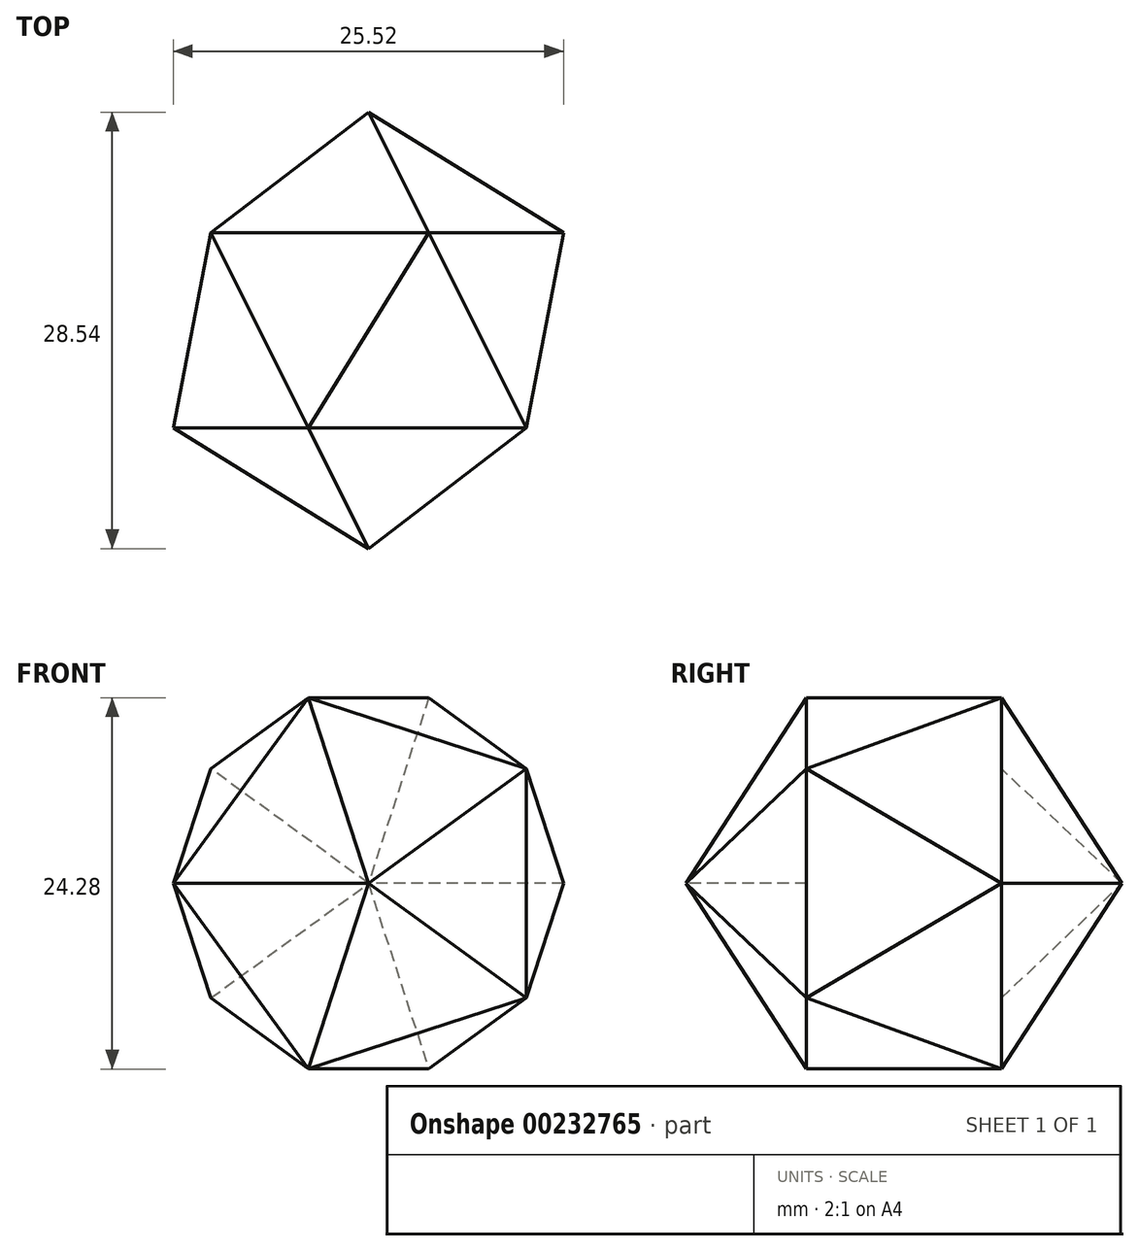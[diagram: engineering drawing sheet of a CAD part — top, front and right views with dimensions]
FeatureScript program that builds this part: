
annotation { "Feature Type Name" : "Feature", "Feature Type Description" : "" }
export const myFeature = defineFeature(function(context is Context, id is Id, definition is map)
    precondition{}
    {
        {
            var Q0;
            Q0=qCreatedBy(makeId("Front.planeOp"),FACE);
            var sketch = newSketch(context, id + "F0", { "sketchPlane" : qUnion([Q0])});
            skCircle(sketch, "E0.cCircle", {"center": v(0, 0) * mm, "radius": 10.32 * mm, "construction": true});
            skLineSegment(sketch, "E0.0", {"start": v(10.32, 7.5) * mm, "end": v(10.32, -7.5) * mm});
            skLineSegment(sketch, "E0.1", {"start": v(10.32, -7.5) * mm, "end": v(-3.94, -12.14) * mm});
            skLineSegment(sketch, "E0.2", {"start": v(-3.94, -12.14) * mm, "end": v(-12.76, 0) * mm});
            skLineSegment(sketch, "E0.3", {"start": v(-12.76, 0) * mm, "end": v(-3.94, 12.14) * mm});
            skLineSegment(sketch, "E0.4", {"start": v(-3.94, 12.14) * mm, "end": v(10.32, 7.5) * mm});
            skPoint(sketch, "E0.0.midPoint", {"position": v(10.32, 0) * mm});
            skSolve(sketch);
        }
        {
            var Q0;
            Q0=qCreatedBy(makeId("Top.planeOp"),FACE);
            var sketch = newSketch(context, id + "F1", { "sketchPlane" : qUnion([Q0])});
            skLineSegment(sketch, "E1", {"start": v(0, -12.43) * mm, "end": v(0, 41.06) * mm, "construction": true});
            skSolve(sketch);
        }
        {
            var Q0;
            Q0=sQuery(id+"F0.wireOp",VERTEX,"E0.1.start");
            var Q1;
            Q1=sQuery(id+"F0.wireOp",VERTEX,"E0.cCircle.center");
            var Q2;
            Q2=sQuery(id+"F1.wireOp",VERTEX,"E1.start");
            cPlane(context, id + "F2", {"entities" : qUnion([Q0, Q1, Q2]), "cplaneType" : CPlaneType.THREE_POINT, "offset" : 25 * mm, "width" : 150 * mm, "height" : 150 * mm});
        }
        {
            var Q0;
            Q0=qCreatedBy(id+"F2.planeOp",FACE);
            var sketch = newSketch(context, id + "F3", { "sketchPlane" : qUnion([Q0])});
            skPoint(sketch, "E2.0", {"position": v(12.76, 0) * mm});
            skLineSegment(sketch, "E3", {"start": v(12.76, 0) * mm, "end": v(0, 7.89) * mm});
            skLineSegment(sketch, "E4.0", {"start": v(0, 12.43) * mm, "end": v(0, -41.06) * mm, "construction": true});
            skSolve(sketch);
        }
        {
            var Q0;
            Q0=qCreatedBy(id+"F2.planeOp",FACE);
            var sketch = newSketch(context, id + "F4", { "sketchPlane" : qUnion([Q0])});
            skPoint(sketch, "E5.1", {"position": v(0, 7.89) * mm});
            skLineSegment(sketch, "E6.0", {"start": v(0, 12.43) * mm, "end": v(0, -41.06) * mm, "construction": true});
            skArc(sketch, "E7", {"start": v(0, -20.65) * mm, "mid": v(14.27, -6.38) * mm, "end": v(0, 7.89) * mm});
            skLineSegment(sketch, "E8", {"start": v(0, 7.89) * mm, "end": v(0, -20.65) * mm});
            skLineSegment(sketch, "E9", {"start": v(23.46, 5.35) * mm, "end": v(-22.52, -17.64) * mm, "construction": true});
            skSolve(sketch);
        }
        {
            var Q0;
            Q0 = qSketchRegion(id + "F4", true);
            var Q1;
            Q1=sQuery(id+"F4.wireOp",EDGE,"E6.0");
            revolve(context, id + "F5", {"entities" : qUnion([Q0]), "axis" : qUnion([Q1]), "revolveType" : RevolveType.FULL});
        }
        {
            var Q0;
            Q0=sQuery(id+"F3.wireOp",VERTEX,"E2.0");
            var Q1;
            Q1=sQuery(id+"F3.wireOp",VERTEX,"E3.end");
            var Q2;
            Q2=sQuery(id+"F0.wireOp",VERTEX,"E0.4.start");
            cPlane(context, id + "F6", {"entities" : qUnion([Q0, Q1, Q2]), "cplaneType" : CPlaneType.THREE_POINT, "offset" : 25 * mm, "width" : 150 * mm, "height" : 150 * mm});
        }
        {
            var Q0;
            Q0=qCreatedBy(id+"F6.planeOp",FACE);
            var sketch = newSketch(context, id + "F7", { "sketchPlane" : qUnion([Q0])});
            skPoint(sketch, "E10.0", {"position": v(5.7, 0) * mm});
            skPoint(sketch, "E11.0", {"position": v(-2.65, -6.07) * mm});
            skCircle(sketch, "E12.cCircle", {"center": v(5.7, 0) * mm, "radius": 10.32 * mm, "construction": true});
            skLineSegment(sketch, "E12.0", {"start": v(1.76, -12.14) * mm, "end": v(-7.05, 0) * mm});
            skLineSegment(sketch, "E12.1", {"start": v(-7.05, 0) * mm, "end": v(1.76, 12.14) * mm});
            skLineSegment(sketch, "E12.2", {"start": v(1.76, 12.14) * mm, "end": v(16.03, 7.5) * mm});
            skLineSegment(sketch, "E12.3", {"start": v(16.03, 7.5) * mm, "end": v(16.03, -7.5) * mm});
            skLineSegment(sketch, "E12.4", {"start": v(16.03, -7.5) * mm, "end": v(1.76, -12.14) * mm});
            skSolve(sketch);
        }
        {
            var Q0;
            Q0=sQuery(id+"F3.wireOp",VERTEX,"E2.0");
            var Q1;
            Q1=sQuery(id+"F7.wireOp",VERTEX,"E12.0.end");
            var Q2;
            Q2=sQuery(id+"F0.wireOp",VERTEX,"E0.3.start");
            cPlane(context, id + "F8", {"entities" : qUnion([Q0, Q1, Q2]), "cplaneType" : CPlaneType.THREE_POINT, "offset" : 25 * mm, "width" : 150 * mm, "height" : 150 * mm});
        }
        {
            var Q0;
            Q0=qCreatedBy(id+"F8.planeOp",FACE);
            var sketch = newSketch(context, id + "F9", { "sketchPlane" : qUnion([Q0])});
            skPoint(sketch, "E13.0", {"position": v(6.38, -1.75) * mm});
            skPoint(sketch, "E13.1", {"position": v(1.01, -6.98) * mm});
            skPoint(sketch, "E14.0", {"position": v(-0.82, 5.65) * mm});
            skCircle(sketch, "E15.cCircle", {"center": v(-0.82, 5.65) * mm, "radius": 10.32 * mm, "construction": true});
            skLineSegment(sketch, "E15.0", {"start": v(11.76, 3.5) * mm, "end": v(1.01, -6.98) * mm});
            skLineSegment(sketch, "E15.1", {"start": v(1.01, -6.98) * mm, "end": v(-12.26, 0) * mm});
            skLineSegment(sketch, "E15.2", {"start": v(-12.26, 0) * mm, "end": v(-9.73, 14.78) * mm});
            skLineSegment(sketch, "E15.3", {"start": v(-9.73, 14.78) * mm, "end": v(5.12, 16.94) * mm});
            skLineSegment(sketch, "E15.4", {"start": v(5.12, 16.94) * mm, "end": v(11.76, 3.5) * mm});
            skSolve(sketch);
        }
        {
            var Q0;
            Q0=sQuery(id+"F9.wireOp",VERTEX,"E15.2.start");
            var Q1;
            Q1=sQuery(id+"F0.wireOp",VERTEX,"E0.2.start");
            var Q2;
            Q2=sQuery(id+"F9.wireOp",VERTEX,"E15.4.start");
            cPlane(context, id + "F10", {"entities" : qUnion([Q0, Q1, Q2]), "cplaneType" : CPlaneType.THREE_POINT, "offset" : 25 * mm, "width" : 150 * mm, "height" : 150 * mm});
        }
        {
            var Q0;
            Q0=qCreatedBy(id+"F10.planeOp",FACE);
            var sketch = newSketch(context, id + "F11", { "sketchPlane" : qUnion([Q0])});
            skPoint(sketch, "E16.0", {"position": v(-5.7, 0) * mm});
            skPoint(sketch, "E17.0", {"position": v(4.62, 0) * mm});
            skCircle(sketch, "E18.cCircle", {"center": v(-5.7, 0) * mm, "radius": 10.32 * mm, "construction": true});
            skLineSegment(sketch, "E18.0", {"start": v(4.62, 7.5) * mm, "end": v(4.62, -7.5) * mm});
            skLineSegment(sketch, "E18.1", {"start": v(4.62, -7.5) * mm, "end": v(-9.65, -12.14) * mm});
            skLineSegment(sketch, "E18.2", {"start": v(-9.65, -12.14) * mm, "end": v(-18.47, 0) * mm});
            skLineSegment(sketch, "E18.3", {"start": v(-18.47, 0) * mm, "end": v(-9.65, 12.14) * mm});
            skLineSegment(sketch, "E18.4", {"start": v(-9.65, 12.14) * mm, "end": v(4.62, 7.5) * mm});
            skSolve(sketch);
        }
        {
            var Q0;
            Q0=sQuery(id+"F0.wireOp",VERTEX,"E0.4.end");
            var Q1;
            Q1=sQuery(id+"F7.wireOp",VERTEX,"E12.2.start");
            var Q2;
            Q2=sQuery(id+"F7.wireOp",VERTEX,"E12.4.start");
            cPlane(context, id + "F12", {"entities" : qUnion([Q0, Q1, Q2]), "cplaneType" : CPlaneType.THREE_POINT, "offset" : 25 * mm, "width" : 150 * mm, "height" : 150 * mm});
        }
        {
            var Q0;
            Q0=qCreatedBy(id+"F12.planeOp",FACE);
            var sketch = newSketch(context, id + "F13", { "sketchPlane" : qUnion([Q0])});
            skPoint(sketch, "E19.0", {"position": v(-0.82, 5.65) * mm});
            skPoint(sketch, "E20.0", {"position": v(0.66, -4.57) * mm});
            skCircle(sketch, "E21.cCircle", {"center": v(-0.82, 5.65) * mm, "radius": 10.32 * mm, "construction": true});
            skLineSegment(sketch, "E21.0", {"start": v(8.09, -3.5) * mm, "end": v(-6.76, -5.65) * mm});
            skLineSegment(sketch, "E21.1", {"start": v(-6.76, -5.65) * mm, "end": v(-13.4, 7.8) * mm});
            skLineSegment(sketch, "E21.2", {"start": v(-13.4, 7.8) * mm, "end": v(-2.66, 18.27) * mm});
            skLineSegment(sketch, "E21.3", {"start": v(-2.66, 18.27) * mm, "end": v(10.62, 11.3) * mm});
            skLineSegment(sketch, "E21.4", {"start": v(10.62, 11.3) * mm, "end": v(8.09, -3.5) * mm});
            skSolve(sketch);
        }
        {
            var Q0;
            Q0=sQuery(id+"F11.wireOp",VERTEX,"E18.2.start");
            var Q1;
            Q1=sQuery(id+"F13.wireOp",VERTEX,"E21.4.start");
            var Q2;
            Q2=sQuery(id+"F7.wireOp",VERTEX,"E12.3.start");
            cPlane(context, id + "F14", {"entities" : qUnion([Q0, Q1, Q2]), "cplaneType" : CPlaneType.THREE_POINT, "offset" : 25 * mm, "width" : 150 * mm, "height" : 150 * mm});
        }
        {
            var Q0;
            Q0=qCreatedBy(id+"F14.planeOp",FACE);
            var sketch = newSketch(context, id + "F15", { "sketchPlane" : qUnion([Q0])});
            skPoint(sketch, "E22.0", {"position": v(0, 0) * mm});
            skPoint(sketch, "E23.0", {"position": v(-8.35, 6.07) * mm});
            skCircle(sketch, "E24.cCircle", {"center": v(0, 0) * mm, "radius": 10.32 * mm, "construction": true});
            skLineSegment(sketch, "E24.0", {"start": v(-12.76, 0) * mm, "end": v(-3.94, 12.14) * mm});
            skLineSegment(sketch, "E24.1", {"start": v(-3.94, 12.14) * mm, "end": v(10.32, 7.5) * mm});
            skLineSegment(sketch, "E24.2", {"start": v(10.32, 7.5) * mm, "end": v(10.32, -7.5) * mm});
            skLineSegment(sketch, "E24.3", {"start": v(10.32, -7.5) * mm, "end": v(-3.94, -12.14) * mm});
            skLineSegment(sketch, "E24.4", {"start": v(-3.94, -12.14) * mm, "end": v(-12.76, 0) * mm});
            skSolve(sketch);
        }
        {
            var Q0;
            Q0=sQuery(id+"F9.wireOp",VERTEX,"E13.1");
            var Q1;
            Q1=sQuery(id+"F13.wireOp",VERTEX,"E21.0.start");
            var Q2;
            Q2=sQuery(id+"F15.wireOp",VERTEX,"E24.1.start");
            cPlane(context, id + "F16", {"entities" : qUnion([Q0, Q1, Q2]), "cplaneType" : CPlaneType.THREE_POINT, "offset" : 25 * mm, "width" : 150 * mm, "height" : 150 * mm});
        }
        {
            var Q0;
            Q0=qCreatedBy(id+"F16.planeOp",FACE);
            var sketch = newSketch(context, id + "F17", { "sketchPlane" : qUnion([Q0])});
            skPoint(sketch, "E25.0", {"position": v(-0.82, -5.65) * mm});
            skPoint(sketch, "E26.0", {"position": v(-2.3, -15.86) * mm});
            skCircle(sketch, "E27.cCircle", {"center": v(-0.82, -5.65) * mm, "radius": 10.32 * mm, "construction": true});
            skLineSegment(sketch, "E27.0", {"start": v(5.12, -16.94) * mm, "end": v(-9.73, -14.78) * mm});
            skLineSegment(sketch, "E27.1", {"start": v(-9.73, -14.78) * mm, "end": v(-12.26, 0) * mm});
            skLineSegment(sketch, "E27.2", {"start": v(-12.26, 0) * mm, "end": v(1.01, 6.98) * mm});
            skLineSegment(sketch, "E27.3", {"start": v(1.01, 6.98) * mm, "end": v(11.76, -3.5) * mm});
            skLineSegment(sketch, "E27.4", {"start": v(11.76, -3.5) * mm, "end": v(5.12, -16.94) * mm});
            skSolve(sketch);
        }
        {
            var Q0;
            Q0=sQuery(id+"F9.wireOp",VERTEX,"E13.1");
            var Q1;
            Q1=sQuery(id+"F11.wireOp",VERTEX,"E18.1.start");
            var Q2;
            Q2=sQuery(id+"F15.wireOp",VERTEX,"E24.3.start");
            cPlane(context, id + "F18", {"entities" : qUnion([Q0, Q1, Q2]), "cplaneType" : CPlaneType.THREE_POINT, "offset" : 25 * mm, "width" : 150 * mm, "height" : 150 * mm});
        }
        {
            var Q0;
            Q0=qCreatedBy(id+"F18.planeOp",FACE);
            var sketch = newSketch(context, id + "F19", { "sketchPlane" : qUnion([Q0])});
            skPoint(sketch, "E28.0", {"position": v(-5.7, 0) * mm});
            skPoint(sketch, "E29.0", {"position": v(-16.03, 0) * mm});
            skCircle(sketch, "E30.cCircle", {"center": v(-5.7, 0) * mm, "radius": 10.32 * mm, "construction": true});
            skLineSegment(sketch, "E30.0", {"start": v(-16.03, -7.5) * mm, "end": v(-16.03, 7.5) * mm});
            skLineSegment(sketch, "E30.1", {"start": v(-16.03, 7.5) * mm, "end": v(-1.76, 12.14) * mm});
            skLineSegment(sketch, "E30.2", {"start": v(-1.76, 12.14) * mm, "end": v(7.05, 0) * mm});
            skLineSegment(sketch, "E30.3", {"start": v(7.05, 0) * mm, "end": v(-1.76, -12.14) * mm});
            skLineSegment(sketch, "E30.4", {"start": v(-1.76, -12.14) * mm, "end": v(-16.03, -7.5) * mm});
            skSolve(sketch);
        }
        {
            var Q0;
            Q0=sQuery(id+"F13.wireOp",VERTEX,"E21.3.start");
            var Q1;
            Q1=sQuery(id+"F17.wireOp",VERTEX,"E27.4.end");
            var Q2;
            Q2=sQuery(id+"F19.wireOp",VERTEX,"E30.4.end");
            cPlane(context, id + "F20", {"entities" : qUnion([Q0, Q1, Q2]), "cplaneType" : CPlaneType.THREE_POINT, "offset" : 25 * mm, "width" : 150 * mm, "height" : 150 * mm});
        }
        {
            var Q0;
            Q0=qCreatedBy(id+"F20.planeOp",FACE);
            var sketch = newSketch(context, id + "F21", { "sketchPlane" : qUnion([Q0])});
            skPoint(sketch, "E31.0", {"position": v(-2.52, 9.82) * mm});
            skPoint(sketch, "E32.0", {"position": v(-5.7, 0) * mm});
            skCircle(sketch, "E33.cCircle", {"center": v(-5.7, 0) * mm, "radius": 10.32 * mm, "construction": true});
            skLineSegment(sketch, "E33.0", {"start": v(-9.65, 12.14) * mm, "end": v(4.62, 7.5) * mm});
            skLineSegment(sketch, "E33.1", {"start": v(4.62, 7.5) * mm, "end": v(4.62, -7.5) * mm});
            skLineSegment(sketch, "E33.2", {"start": v(4.62, -7.5) * mm, "end": v(-9.65, -12.14) * mm});
            skLineSegment(sketch, "E33.3", {"start": v(-9.65, -12.14) * mm, "end": v(-18.47, 0) * mm});
            skLineSegment(sketch, "E33.4", {"start": v(-18.47, 0) * mm, "end": v(-9.65, 12.14) * mm});
            skSolve(sketch);
        }
        {
            var Q0;
            Q0=qCreatedBy(id+"F2.planeOp",FACE);
            var sketch = newSketch(context, id + "F22", { "sketchPlane" : qUnion([Q0])});
            skLineSegment(sketch, "E34", {"start": v(21.42, -5.35) * mm, "end": v(-16.22, 17.91) * mm});
            skLineSegment(sketch, "E35", {"start": v(21.42, -5.35) * mm, "end": v(21.42, 17.91) * mm});
            skLineSegment(sketch, "E36", {"start": v(21.42, 17.91) * mm, "end": v(-16.22, 17.91) * mm});
            skSolve(sketch);
        }
        {
            var Q0;
            Q0 = qSketchRegion(id + "F22", true);
            extrude(context, id + "F23", {"entities" : qUnion([Q0]), "endBound" : BoundingType.THROUGH_ALL, "depth" : 25 * mm, "hasSecondDirection" : true, "secondDirectionBound" : SecondDirectionBoundingType.THROUGH_ALL, "secondDirectionOppositeDirection" : true, "secondDirectionDepth" : 25 * mm});
        }
        {
            var Q0;
            Q0=makeQuery(id+"F23.opExtrude","SWEPT_BODY",BODY,{"disambiguationData":[OSD([sQuery(id+"F22.wireOp",EDGE,"E34"),sQuery(id+"F22.wireOp",EDGE,"E35"),sQuery(id+"F22.wireOp",EDGE,"E36")])]});
            var Q1;
            Q1=sQuery(id+"F1.wireOp",EDGE,"E1");
            circularPattern(context, id + "F24", {"entities" : qUnion([Q0]), "axis" : qUnion([Q1]), "angle" : 360 * degree, "instanceCount" : 5, "oppositeDirection" : true, "equalSpace" : true});
        }
        {
            var Q0;
            Q0=makeQuery(id+"F23.opExtrude","SWEPT_BODY",BODY,{"disambiguationData":[OSD([sQuery(id+"F22.wireOp",EDGE,"E34"),sQuery(id+"F22.wireOp",EDGE,"E35"),sQuery(id+"F22.wireOp",EDGE,"E36")])]});
            var Q1;
            Q1=makeQuery(id+"F24.opPattern","COPY",BODY,{"derivedFrom":makeQuery(id+"F23.opExtrude","SWEPT_BODY",BODY,{"disambiguationData":[OSD([sQuery(id+"F22.wireOp",EDGE,"E34"),sQuery(id+"F22.wireOp",EDGE,"E35"),sQuery(id+"F22.wireOp",EDGE,"E36")])]}),"instanceName":"1"});
            var Q2;
            Q2=makeQuery(id+"F24.opPattern","COPY",BODY,{"derivedFrom":makeQuery(id+"F23.opExtrude","SWEPT_BODY",BODY,{"disambiguationData":[OSD([sQuery(id+"F22.wireOp",EDGE,"E34"),sQuery(id+"F22.wireOp",EDGE,"E35"),sQuery(id+"F22.wireOp",EDGE,"E36")])]}),"instanceName":"2"});
            var Q3;
            Q3=makeQuery(id+"F24.opPattern","COPY",BODY,{"derivedFrom":makeQuery(id+"F23.opExtrude","SWEPT_BODY",BODY,{"disambiguationData":[OSD([sQuery(id+"F22.wireOp",EDGE,"E34"),sQuery(id+"F22.wireOp",EDGE,"E35"),sQuery(id+"F22.wireOp",EDGE,"E36")])]}),"instanceName":"3"});
            var Q4;
            Q4=makeQuery(id+"F24.opPattern","COPY",BODY,{"derivedFrom":makeQuery(id+"F23.opExtrude","SWEPT_BODY",BODY,{"disambiguationData":[OSD([sQuery(id+"F22.wireOp",EDGE,"E34"),sQuery(id+"F22.wireOp",EDGE,"E35"),sQuery(id+"F22.wireOp",EDGE,"E36")])]}),"instanceName":"4"});
            var Q5;
            Q5=makeQuery(id+"F5.opRevolve","SWEPT_BODY",BODY,{"disambiguationData":[OSD([sQuery(id+"F4.wireOp",EDGE,"E7"),sQuery(id+"F4.wireOp",EDGE,"E8")])]});
            booleanBodies(context, id + "F25", {"operationType" : BooleanOperationType.SUBTRACTION, "tools" : qUnion([Q0, Q1, Q2, Q3, Q4]), "targets" : qUnion([Q5])});
        }
        {
            var Q0;
            Q0=sQuery(id+"F21.wireOp",VERTEX,"E31.0");
            var Q1;
            Q1=sQuery(id+"F19.wireOp",VERTEX,"E30.1.start");
            var Q2;
            Q2=sQuery(id+"F4.wireOp",VERTEX,"E7.center");
            cPlane(context, id + "F26", {"entities" : qUnion([Q0, Q1, Q2]), "cplaneType" : CPlaneType.THREE_POINT, "offset" : 25 * mm, "width" : 150 * mm, "height" : 150 * mm});
        }
        {
            var Q0;
            Q0=qCreatedBy(id+"F26.planeOp",FACE);
            var sketch = newSketch(context, id + "F27", { "sketchPlane" : qUnion([Q0])});
            skPoint(sketch, "E37.0", {"position": v(15.49, 7.5) * mm});
            skPoint(sketch, "E37.1", {"position": v(3.35, 12.14) * mm});
            skLineSegment(sketch, "E38", {"start": v(21.27, 5.3) * mm, "end": v(-6.84, 16.03) * mm});
            skLineSegment(sketch, "E39", {"start": v(-6.84, 16.03) * mm, "end": v(12.96, 27.94) * mm});
            skLineSegment(sketch, "E40", {"start": v(12.96, 27.94) * mm, "end": v(21.27, 5.3) * mm});
            skSolve(sketch);
        }
        {
            var Q0;
            Q0 = qSketchRegion(id + "F27", true);
            extrude(context, id + "F28", {"entities" : qUnion([Q0]), "endBound" : BoundingType.THROUGH_ALL, "depth" : 25 * mm, "hasSecondDirection" : true, "secondDirectionBound" : SecondDirectionBoundingType.THROUGH_ALL, "secondDirectionOppositeDirection" : true, "secondDirectionDepth" : 25 * mm});
        }
        {
            var Q0;
            Q0=makeQuery(id+"F28.opExtrude","SWEPT_BODY",BODY,{"disambiguationData":[OSD([sQuery(id+"F27.wireOp",EDGE,"E38"),sQuery(id+"F27.wireOp",EDGE,"E39"),sQuery(id+"F27.wireOp",EDGE,"E40")])]});
            var Q1;
            Q1=sQuery(id+"F4.wireOp",EDGE,"E9");
            circularPattern(context, id + "F29", {"entities" : qUnion([Q0]), "axis" : qUnion([Q1]), "angle" : 360 * degree, "instanceCount" : 5, "equalSpace" : true});
        }
        {
            var Q0;
            Q0=makeQuery(id+"F28.opExtrude","SWEPT_BODY",BODY,{"disambiguationData":[OSD([sQuery(id+"F27.wireOp",EDGE,"E38"),sQuery(id+"F27.wireOp",EDGE,"E39"),sQuery(id+"F27.wireOp",EDGE,"E40")])]});
            var Q1;
            Q1=makeQuery(id+"F29.opPattern","COPY",BODY,{"derivedFrom":makeQuery(id+"F28.opExtrude","SWEPT_BODY",BODY,{"disambiguationData":[OSD([sQuery(id+"F27.wireOp",EDGE,"E38"),sQuery(id+"F27.wireOp",EDGE,"E39"),sQuery(id+"F27.wireOp",EDGE,"E40")])]}),"instanceName":"1"});
            var Q2;
            Q2=makeQuery(id+"F29.opPattern","COPY",BODY,{"derivedFrom":makeQuery(id+"F28.opExtrude","SWEPT_BODY",BODY,{"disambiguationData":[OSD([sQuery(id+"F27.wireOp",EDGE,"E38"),sQuery(id+"F27.wireOp",EDGE,"E39"),sQuery(id+"F27.wireOp",EDGE,"E40")])]}),"instanceName":"2"});
            var Q3;
            Q3=makeQuery(id+"F29.opPattern","COPY",BODY,{"derivedFrom":makeQuery(id+"F28.opExtrude","SWEPT_BODY",BODY,{"disambiguationData":[OSD([sQuery(id+"F27.wireOp",EDGE,"E38"),sQuery(id+"F27.wireOp",EDGE,"E39"),sQuery(id+"F27.wireOp",EDGE,"E40")])]}),"instanceName":"3"});
            var Q4;
            Q4=makeQuery(id+"F29.opPattern","COPY",BODY,{"derivedFrom":makeQuery(id+"F28.opExtrude","SWEPT_BODY",BODY,{"disambiguationData":[OSD([sQuery(id+"F27.wireOp",EDGE,"E38"),sQuery(id+"F27.wireOp",EDGE,"E39"),sQuery(id+"F27.wireOp",EDGE,"E40")])]}),"instanceName":"4"});
            var Q5;
            Q5=makeQuery(id+"F5.opRevolve","SWEPT_BODY",BODY,{"disambiguationData":[OSD([sQuery(id+"F4.wireOp",EDGE,"E7"),sQuery(id+"F4.wireOp",EDGE,"E8")])]});
            booleanBodies(context, id + "F30", {"operationType" : BooleanOperationType.SUBTRACTION, "tools" : qUnion([Q0, Q1, Q2, Q3, Q4]), "targets" : qUnion([Q5])});
        }
        {
            var Q0;
            Q0=sQuery(id+"F21.wireOp",EDGE,"E33.3");
            cPoint(context, id + "F31", {"entities" : qUnion([Q0]), "parameter" : 0.5});
        }
        {
            var Q0;
            Q0=sQuery(id+"F15.wireOp",VERTEX,"E24.4.start");
            var Q1;
            Q1=sQuery(id+"F7.wireOp",VERTEX,"E12.1.end");
            var Q2;
            Q2 = qCreatedBy(id + "F31" ,VERTEX);
            cPlane(context, id + "F32", {"entities" : qUnion([Q0, Q1, Q2]), "cplaneType" : CPlaneType.THREE_POINT, "offset" : 25 * mm, "width" : 150 * mm, "height" : 150 * mm});
        }
        {
            var Q0;
            Q0=qCreatedBy(id+"F32.planeOp",FACE);
            var sketch = newSketch(context, id + "F33", { "sketchPlane" : qUnion([Q0])});
            skLineSegment(sketch, "E41", {"start": v(21.48, -25.98) * mm, "end": v(-9.12, 23.53) * mm, "construction": true});
            skPoint(sketch, "E42.0", {"position": v(-2.07, 12.14) * mm});
            skPoint(sketch, "E42.1", {"position": v(12.93, -12.14) * mm});
            skPoint(sketch, "E42.2", {"position": v(17.56, 0) * mm});
            skLineSegment(sketch, "E43", {"start": v(9.83, -20.23) * mm, "end": v(20.6, 7.93) * mm});
            skLineSegment(sketch, "E44", {"start": v(9.83, -20.23) * mm, "end": v(20.6, -20.23) * mm});
            skLineSegment(sketch, "E45", {"start": v(20.6, -20.23) * mm, "end": v(20.6, 7.93) * mm});
            skSolve(sketch);
        }
        {
            var Q0;
            Q0 = qSketchRegion(id + "F33", true);
            extrude(context, id + "F34", {"entities" : qUnion([Q0]), "endBound" : BoundingType.THROUGH_ALL, "depth" : 25 * mm, "hasSecondDirection" : true, "secondDirectionBound" : SecondDirectionBoundingType.THROUGH_ALL, "secondDirectionOppositeDirection" : true, "secondDirectionDepth" : 25 * mm});
        }
        {
            var Q0;
            Q0=makeQuery(id+"F34.opExtrude","SWEPT_BODY",BODY,{"disambiguationData":[OSD([sQuery(id+"F33.wireOp",EDGE,"E43"),sQuery(id+"F33.wireOp",EDGE,"E44"),sQuery(id+"F33.wireOp",EDGE,"E45")])]});
            var Q1;
            Q1=sQuery(id+"F4.wireOp",EDGE,"E6.0");
            circularPattern(context, id + "F35", {"entities" : qUnion([Q0]), "axis" : qUnion([Q1]), "angle" : 360 * degree, "instanceCount" : 5, "equalSpace" : true});
        }
        {
            var Q0;
            Q0=makeQuery(id+"F34.opExtrude","SWEPT_BODY",BODY,{"disambiguationData":[OSD([sQuery(id+"F33.wireOp",EDGE,"E43"),sQuery(id+"F33.wireOp",EDGE,"E44"),sQuery(id+"F33.wireOp",EDGE,"E45")])]});
            var Q1;
            Q1=makeQuery(id+"F35.opPattern","COPY",BODY,{"derivedFrom":makeQuery(id+"F34.opExtrude","SWEPT_BODY",BODY,{"disambiguationData":[OSD([sQuery(id+"F33.wireOp",EDGE,"E43"),sQuery(id+"F33.wireOp",EDGE,"E44"),sQuery(id+"F33.wireOp",EDGE,"E45")])]}),"instanceName":"1"});
            var Q2;
            Q2=makeQuery(id+"F35.opPattern","COPY",BODY,{"derivedFrom":makeQuery(id+"F34.opExtrude","SWEPT_BODY",BODY,{"disambiguationData":[OSD([sQuery(id+"F33.wireOp",EDGE,"E43"),sQuery(id+"F33.wireOp",EDGE,"E44"),sQuery(id+"F33.wireOp",EDGE,"E45")])]}),"instanceName":"2"});
            var Q3;
            Q3=makeQuery(id+"F35.opPattern","COPY",BODY,{"derivedFrom":makeQuery(id+"F34.opExtrude","SWEPT_BODY",BODY,{"disambiguationData":[OSD([sQuery(id+"F33.wireOp",EDGE,"E43"),sQuery(id+"F33.wireOp",EDGE,"E44"),sQuery(id+"F33.wireOp",EDGE,"E45")])]}),"instanceName":"3"});
            var Q4;
            Q4=makeQuery(id+"F35.opPattern","COPY",BODY,{"derivedFrom":makeQuery(id+"F34.opExtrude","SWEPT_BODY",BODY,{"disambiguationData":[OSD([sQuery(id+"F33.wireOp",EDGE,"E43"),sQuery(id+"F33.wireOp",EDGE,"E44"),sQuery(id+"F33.wireOp",EDGE,"E45")])]}),"instanceName":"4"});
            var Q5;
            Q5=makeQuery(id+"F5.opRevolve","SWEPT_BODY",BODY,{"disambiguationData":[OSD([sQuery(id+"F4.wireOp",EDGE,"E7"),sQuery(id+"F4.wireOp",EDGE,"E8")])]});
            booleanBodies(context, id + "F36", {"operationType" : BooleanOperationType.SUBTRACTION, "tools" : qUnion([Q0, Q1, Q2, Q3, Q4]), "targets" : qUnion([Q5])});
        }
        {
            var Q0;
            Q0=sQuery(id+"F11.wireOp",EDGE,"E18.1");
            cPoint(context, id + "F37", {"entities" : qUnion([Q0]), "parameter" : 0.5});
        }
        {
            var Q0;
            Q0=sQuery(id+"F3.wireOp",VERTEX,"E2.0");
            var Q1;
            Q1=sQuery(id+"F19.wireOp",VERTEX,"E30.1.start");
            var Q2;
            Q2 = qCreatedBy(id + "F37" ,VERTEX);
            cPlane(context, id + "F38", {"entities" : qUnion([Q0, Q1, Q2]), "cplaneType" : CPlaneType.THREE_POINT, "offset" : 25 * mm, "width" : 150 * mm, "height" : 150 * mm});
        }
        {
            var Q0;
            Q0=qCreatedBy(id+"F38.planeOp",FACE);
            var sketch = newSketch(context, id + "F39", { "sketchPlane" : qUnion([Q0])});
            skPoint(sketch, "E46.0", {"position": v(-8.78, -7.5) * mm});
            skPoint(sketch, "E46.1", {"position": v(3.35, -12.14) * mm});
            skLineSegment(sketch, "E47", {"start": v(24.85, -20.35) * mm, "end": v(-19.98, -3.22) * mm});
            skLineSegment(sketch, "E48", {"start": v(-19.98, -3.22) * mm, "end": v(-19.98, -20.35) * mm});
            skLineSegment(sketch, "E49", {"start": v(-19.98, -20.35) * mm, "end": v(24.85, -20.35) * mm});
            skSolve(sketch);
        }
        {
            var Q0;
            Q0 = qSketchRegion(id + "F39", true);
            extrude(context, id + "F40", {"entities" : qUnion([Q0]), "endBound" : BoundingType.THROUGH_ALL, "depth" : 25 * mm, "hasSecondDirection" : true, "secondDirectionBound" : SecondDirectionBoundingType.THROUGH_ALL, "secondDirectionOppositeDirection" : true, "secondDirectionDepth" : 25 * mm});
        }
        {
            var Q0;
            Q0=makeQuery(id+"F40.opExtrude","SWEPT_BODY",BODY,{"disambiguationData":[OSD([sQuery(id+"F39.wireOp",EDGE,"E47"),sQuery(id+"F39.wireOp",EDGE,"E48"),sQuery(id+"F39.wireOp",EDGE,"E49")])]});
            var Q1;
            Q1=sQuery(id+"F4.wireOp",EDGE,"E9");
            circularPattern(context, id + "F41", {"entities" : qUnion([Q0]), "axis" : qUnion([Q1]), "angle" : 360 * degree, "instanceCount" : 5, "equalSpace" : true});
        }
        {
            var Q0;
            Q0=makeQuery(id+"F40.opExtrude","SWEPT_BODY",BODY,{"disambiguationData":[OSD([sQuery(id+"F39.wireOp",EDGE,"E47"),sQuery(id+"F39.wireOp",EDGE,"E48"),sQuery(id+"F39.wireOp",EDGE,"E49")])]});
            var Q1;
            Q1=makeQuery(id+"F41.opPattern","COPY",BODY,{"derivedFrom":makeQuery(id+"F40.opExtrude","SWEPT_BODY",BODY,{"disambiguationData":[OSD([sQuery(id+"F39.wireOp",EDGE,"E47"),sQuery(id+"F39.wireOp",EDGE,"E48"),sQuery(id+"F39.wireOp",EDGE,"E49")])]}),"instanceName":"1"});
            var Q2;
            Q2=makeQuery(id+"F41.opPattern","COPY",BODY,{"derivedFrom":makeQuery(id+"F40.opExtrude","SWEPT_BODY",BODY,{"disambiguationData":[OSD([sQuery(id+"F39.wireOp",EDGE,"E47"),sQuery(id+"F39.wireOp",EDGE,"E48"),sQuery(id+"F39.wireOp",EDGE,"E49")])]}),"instanceName":"2"});
            var Q3;
            Q3=makeQuery(id+"F41.opPattern","COPY",BODY,{"derivedFrom":makeQuery(id+"F40.opExtrude","SWEPT_BODY",BODY,{"disambiguationData":[OSD([sQuery(id+"F39.wireOp",EDGE,"E47"),sQuery(id+"F39.wireOp",EDGE,"E48"),sQuery(id+"F39.wireOp",EDGE,"E49")])]}),"instanceName":"3"});
            var Q4;
            Q4=makeQuery(id+"F41.opPattern","COPY",BODY,{"derivedFrom":makeQuery(id+"F40.opExtrude","SWEPT_BODY",BODY,{"disambiguationData":[OSD([sQuery(id+"F39.wireOp",EDGE,"E47"),sQuery(id+"F39.wireOp",EDGE,"E48"),sQuery(id+"F39.wireOp",EDGE,"E49")])]}),"instanceName":"4"});
            var Q5;
            Q5=makeQuery(id+"F5.opRevolve","SWEPT_BODY",BODY,{"disambiguationData":[OSD([sQuery(id+"F4.wireOp",EDGE,"E7"),sQuery(id+"F4.wireOp",EDGE,"E8")])]});
            booleanBodies(context, id + "F42", {"operationType" : BooleanOperationType.SUBTRACTION, "tools" : qUnion([Q0, Q1, Q2, Q3, Q4]), "targets" : qUnion([Q5])});
        }
        {
            var Q0;
            Q0=sQuery(id+"F15.wireOp",EDGE,"E24.3");
            cPoint(context, id + "F43", {"entities" : qUnion([Q0]), "parameter" : 0.5});
        }
        {
            var Q0;
            Q0=sQuery(id+"F19.wireOp",VERTEX,"E30.4.start");
            var Q1;
            Q1=sQuery(id+"F21.wireOp",VERTEX,"E33.4.end");
            var Q2;
            Q2 = qCreatedBy(id + "F43" ,VERTEX);
            cPlane(context, id + "F44", {"entities" : qUnion([Q0, Q1, Q2]), "cplaneType" : CPlaneType.THREE_POINT, "offset" : 25 * mm, "width" : 150 * mm, "height" : 150 * mm});
        }
        {
            var Q0;
            Q0=qCreatedBy(id+"F44.planeOp",FACE);
            var sketch = newSketch(context, id + "F45", { "sketchPlane" : qUnion([Q0])});
            skPoint(sketch, "E50.0", {"position": v(0, -12.76) * mm});
            skPoint(sketch, "E50.1", {"position": v(12.76, 12.76) * mm});
            skPoint(sketch, "E50.2", {"position": v(12.76, -10.32) * mm});
            skLineSegment(sketch, "E51", {"start": v(-5.13, -13.74) * mm, "end": v(23.03, -8.36) * mm});
            skLineSegment(sketch, "E52", {"start": v(23.03, -8.36) * mm, "end": v(9.61, -28.25) * mm});
            skLineSegment(sketch, "E53", {"start": v(9.61, -28.25) * mm, "end": v(-5.13, -13.74) * mm});
            skLineSegment(sketch, "E54", {"start": v(-5.13, -23.03) * mm, "end": v(14, 15.24) * mm, "construction": true});
            skSolve(sketch);
        }
        {
            var Q0;
            Q0=makeQuery(id+"F45.imprint","IMPRINT",FACE,{"disambiguationData":[TD([[makeQuery(id+"F45.imprint","IMPRINT",EDGE,{"derivedFrom":sQuery(id+"F45.wireOp",EDGE,"E51")}),-1.0]])]});
            var Q1;
            Q1=sQuery(id+"F45.wireOp",EDGE,"E53");
            extrude(context, id + "F46", {"entities" : qUnion([Q0]), "surfaceEntities" : qUnion([Q1]), "endBound" : BoundingType.THROUGH_ALL, "depth" : 25 * mm, "hasSecondDirection" : true, "secondDirectionBound" : SecondDirectionBoundingType.THROUGH_ALL, "secondDirectionOppositeDirection" : true, "secondDirectionDepth" : 25 * mm});
        }
        {
            var Q0;
            Q0=makeQuery(id+"F46.opExtrude","SWEPT_BODY",BODY,{"disambiguationData":[OSD([sQuery(id+"F45.wireOp",EDGE,"E51"),sQuery(id+"F45.wireOp",EDGE,"E52"),sQuery(id+"F45.wireOp",EDGE,"E53")])]});
            var Q1;
            Q1=sQuery(id+"F45.wireOp",EDGE,"E54");
            circularPattern(context, id + "F47", {"entities" : qUnion([Q0]), "axis" : qUnion([Q1]), "angle" : 360 * degree, "instanceCount" : 5, "equalSpace" : true});
        }
        {
            var Q0;
            Q0=makeQuery(id+"F46.opExtrude","SWEPT_BODY",BODY,{"disambiguationData":[OSD([sQuery(id+"F45.wireOp",EDGE,"E51"),sQuery(id+"F45.wireOp",EDGE,"E52"),sQuery(id+"F45.wireOp",EDGE,"E53")])]});
            var Q1;
            Q1=makeQuery(id+"F47.opPattern","COPY",BODY,{"derivedFrom":makeQuery(id+"F46.opExtrude","SWEPT_BODY",BODY,{"disambiguationData":[OSD([sQuery(id+"F45.wireOp",EDGE,"E51"),sQuery(id+"F45.wireOp",EDGE,"E52"),sQuery(id+"F45.wireOp",EDGE,"E53")])]}),"instanceName":"1"});
            var Q2;
            Q2=makeQuery(id+"F47.opPattern","COPY",BODY,{"derivedFrom":makeQuery(id+"F46.opExtrude","SWEPT_BODY",BODY,{"disambiguationData":[OSD([sQuery(id+"F45.wireOp",EDGE,"E51"),sQuery(id+"F45.wireOp",EDGE,"E52"),sQuery(id+"F45.wireOp",EDGE,"E53")])]}),"instanceName":"2"});
            var Q3;
            Q3=makeQuery(id+"F47.opPattern","COPY",BODY,{"derivedFrom":makeQuery(id+"F46.opExtrude","SWEPT_BODY",BODY,{"disambiguationData":[OSD([sQuery(id+"F45.wireOp",EDGE,"E51"),sQuery(id+"F45.wireOp",EDGE,"E52"),sQuery(id+"F45.wireOp",EDGE,"E53")])]}),"instanceName":"3"});
            var Q4;
            Q4=makeQuery(id+"F47.opPattern","COPY",BODY,{"derivedFrom":makeQuery(id+"F46.opExtrude","SWEPT_BODY",BODY,{"disambiguationData":[OSD([sQuery(id+"F45.wireOp",EDGE,"E51"),sQuery(id+"F45.wireOp",EDGE,"E52"),sQuery(id+"F45.wireOp",EDGE,"E53")])]}),"instanceName":"4"});
            var Q5;
            Q5=makeQuery(id+"F5.opRevolve","SWEPT_BODY",BODY,{"disambiguationData":[OSD([sQuery(id+"F4.wireOp",EDGE,"E7"),sQuery(id+"F4.wireOp",EDGE,"E8")])]});
            booleanBodies(context, id + "F48", {"operationType" : BooleanOperationType.SUBTRACTION, "tools" : qUnion([Q0, Q1, Q2, Q3, Q4]), "targets" : qUnion([Q5])});
        }
        {
            var Q0;
            Q0=sQuery(id+"F15.wireOp",VERTEX,"E23.0");
            var Q1;
            Q1=sQuery(id+"F17.wireOp",VERTEX,"E27.4.start");
            var Q2;
            Q2=sQuery(id+"F21.wireOp",VERTEX,"E33.3.start");
            cPlane(context, id + "F49", {"entities" : qUnion([Q0, Q1, Q2]), "cplaneType" : CPlaneType.THREE_POINT, "offset" : 25 * mm, "width" : 150 * mm, "height" : 150 * mm});
        }
        {
            var Q0;
            Q0=qCreatedBy(id+"F49.planeOp",FACE);
            var sketch = newSketch(context, id + "F50", { "sketchPlane" : qUnion([Q0])});
            skPoint(sketch, "E55.0", {"position": v(10.32, 12.76) * mm});
            skPoint(sketch, "E55.1", {"position": v(12.76, 0) * mm});
            skPoint(sketch, "E55.2", {"position": v(-12.76, 12.76) * mm});
            skLineSegment(sketch, "E56", {"start": v(19.54, -3.4) * mm, "end": v(-20.52, 16.64) * mm, "construction": true});
            skLineSegment(sketch, "E57", {"start": v(15.65, -15.12) * mm, "end": v(6.87, 30.86) * mm});
            skLineSegment(sketch, "E58", {"start": v(15.65, -15.12) * mm, "end": v(30.89, 8.12) * mm});
            skLineSegment(sketch, "E59", {"start": v(30.89, 8.12) * mm, "end": v(6.87, 30.86) * mm});
            skSolve(sketch);
        }
        {
            var Q0;
            Q0 = qSketchRegion(id + "F50", true);
            extrude(context, id + "F51", {"entities" : qUnion([Q0]), "endBound" : BoundingType.THROUGH_ALL, "depth" : 25 * mm, "hasSecondDirection" : true, "secondDirectionBound" : SecondDirectionBoundingType.THROUGH_ALL, "secondDirectionOppositeDirection" : true, "secondDirectionDepth" : 25 * mm});
        }
        {
            var Q0;
            Q0=makeQuery(id+"F51.opExtrude","SWEPT_BODY",BODY,{"disambiguationData":[OSD([sQuery(id+"F50.wireOp",EDGE,"E57"),sQuery(id+"F50.wireOp",EDGE,"E58"),sQuery(id+"F50.wireOp",EDGE,"E59")])]});
            var Q1;
            Q1=sQuery(id+"F50.wireOp",EDGE,"E56");
            circularPattern(context, id + "F52", {"entities" : qUnion([Q0]), "axis" : qUnion([Q1]), "angle" : 360 * degree, "instanceCount" : 5, "equalSpace" : true});
        }
        {
            var Q0;
            Q0=makeQuery(id+"F51.opExtrude","SWEPT_BODY",BODY,{"disambiguationData":[OSD([sQuery(id+"F50.wireOp",EDGE,"E57"),sQuery(id+"F50.wireOp",EDGE,"E58"),sQuery(id+"F50.wireOp",EDGE,"E59")])]});
            var Q1;
            Q1=makeQuery(id+"F52.opPattern","COPY",BODY,{"derivedFrom":makeQuery(id+"F51.opExtrude","SWEPT_BODY",BODY,{"disambiguationData":[OSD([sQuery(id+"F50.wireOp",EDGE,"E57"),sQuery(id+"F50.wireOp",EDGE,"E58"),sQuery(id+"F50.wireOp",EDGE,"E59")])]}),"instanceName":"1"});
            var Q2;
            Q2=makeQuery(id+"F52.opPattern","COPY",BODY,{"derivedFrom":makeQuery(id+"F51.opExtrude","SWEPT_BODY",BODY,{"disambiguationData":[OSD([sQuery(id+"F50.wireOp",EDGE,"E57"),sQuery(id+"F50.wireOp",EDGE,"E58"),sQuery(id+"F50.wireOp",EDGE,"E59")])]}),"instanceName":"2"});
            var Q3;
            Q3=makeQuery(id+"F52.opPattern","COPY",BODY,{"derivedFrom":makeQuery(id+"F51.opExtrude","SWEPT_BODY",BODY,{"disambiguationData":[OSD([sQuery(id+"F50.wireOp",EDGE,"E57"),sQuery(id+"F50.wireOp",EDGE,"E58"),sQuery(id+"F50.wireOp",EDGE,"E59")])]}),"instanceName":"3"});
            var Q4;
            Q4=makeQuery(id+"F52.opPattern","COPY",BODY,{"derivedFrom":makeQuery(id+"F51.opExtrude","SWEPT_BODY",BODY,{"disambiguationData":[OSD([sQuery(id+"F50.wireOp",EDGE,"E57"),sQuery(id+"F50.wireOp",EDGE,"E58"),sQuery(id+"F50.wireOp",EDGE,"E59")])]}),"instanceName":"4"});
            var Q5;
            Q5=makeQuery(id+"F5.opRevolve","SWEPT_BODY",BODY,{"disambiguationData":[OSD([sQuery(id+"F4.wireOp",EDGE,"E7"),sQuery(id+"F4.wireOp",EDGE,"E8")])]});
            booleanBodies(context, id + "F53", {"operationType" : BooleanOperationType.SUBTRACTION, "tools" : qUnion([Q0, Q1, Q2, Q3, Q4]), "targets" : qUnion([Q5])});
        }
        {
            var Q0;
            {var subQ0=makeQuery(id+"F23.opExtrude","SWEPT_FACE",FACE,{"disambiguationData":[OSD([sQuery(id+"F22.wireOp",EDGE,"E34")])]});Q0=makeQuery(id+"F25.opBoolean","INTERSECT",VERTEX,{"derivedFrom":[subQ0,makeQuery(id+"F24.opPattern","COPY",FACE,{"derivedFrom":subQ0,"instanceName":"1"}),makeQuery(id+"F24.opPattern","COPY",FACE,{"derivedFrom":subQ0,"instanceName":"2"}),makeQuery(id+"F24.opPattern","COPY",FACE,{"derivedFrom":subQ0,"instanceName":"3"}),makeQuery(id+"F24.opPattern","COPY",FACE,{"derivedFrom":subQ0,"instanceName":"4"})]});}
            var Q1;
            {var subQ0=makeQuery(id+"F28.opExtrude","SWEPT_FACE",FACE,{"disambiguationData":[OSD([sQuery(id+"F27.wireOp",EDGE,"E38")])]});Q1=makeQuery(id+"F30.opBoolean","INTERSECT",VERTEX,{"derivedFrom":[makeQuery(id+"F25.opBoolean","COPY",FACE,{"derivedFrom":makeQuery(id+"F24.opPattern","COPY",FACE,{"derivedFrom":makeQuery(id+"F23.opExtrude","SWEPT_FACE",FACE,{"disambiguationData":[OSD([sQuery(id+"F22.wireOp",EDGE,"E34")])]}),"instanceName":"2"})}),makeQuery(id+"F5.opRevolve","SWEPT_FACE",FACE,{"disambiguationData":[OSD([sQuery(id+"F4.wireOp",EDGE,"E7")])]}),subQ0,makeQuery(id+"F29.opPattern","COPY",FACE,{"derivedFrom":subQ0,"instanceName":"4"})]});}
            var Q2;
            {var subQ0=makeQuery(id+"F28.opExtrude","SWEPT_FACE",FACE,{"disambiguationData":[OSD([sQuery(id+"F27.wireOp",EDGE,"E38")])]});Q2=makeQuery(id+"F30.opBoolean","INTERSECT",VERTEX,{"derivedFrom":[makeQuery(id+"F25.opBoolean","COPY",FACE,{"derivedFrom":makeQuery(id+"F24.opPattern","COPY",FACE,{"derivedFrom":makeQuery(id+"F23.opExtrude","SWEPT_FACE",FACE,{"disambiguationData":[OSD([sQuery(id+"F22.wireOp",EDGE,"E34")])]}),"instanceName":"3"})}),makeQuery(id+"F5.opRevolve","SWEPT_FACE",FACE,{"disambiguationData":[OSD([sQuery(id+"F4.wireOp",EDGE,"E7")])]}),makeQuery(id+"F29.opPattern","COPY",FACE,{"derivedFrom":subQ0,"instanceName":"3"}),makeQuery(id+"F29.opPattern","COPY",FACE,{"derivedFrom":subQ0,"instanceName":"4"})]});}
            cPlane(context, id + "F54", {"entities" : qUnion([Q0, Q1, Q2]), "cplaneType" : CPlaneType.THREE_POINT, "offset" : 25 * mm, "width" : 150 * mm, "height" : 150 * mm});
        }
        {
            var Q0;
            Q0=qCreatedBy(id+"F54.planeOp",FACE);
            var sketch = newSketch(context, id + "F55", { "sketchPlane" : qUnion([Q0])});
            skLineSegment(sketch, "E60.0", {"start": v(-3.53, -3.23) * mm, "end": v(1, 11.07) * mm});
            skLineSegment(sketch, "E60.1", {"start": v(11.11, 0) * mm, "end": v(-3.53, -3.23) * mm});
            skLineSegment(sketch, "E61", {"start": v(1, 11.07) * mm, "end": v(11.11, 0) * mm});
            skSolve(sketch);
        }
        {
            var Q0;
            Q0 = qSketchRegion(id + "F55", true);
            extrude(context, id + "F56", {"entities" : qUnion([Q0]), "operationType" : NewBodyOperationType.REMOVE, "endBound" : BoundingType.THROUGH_ALL, "oppositeDirection" : true, "depth" : 25 * mm});
        }
    });
